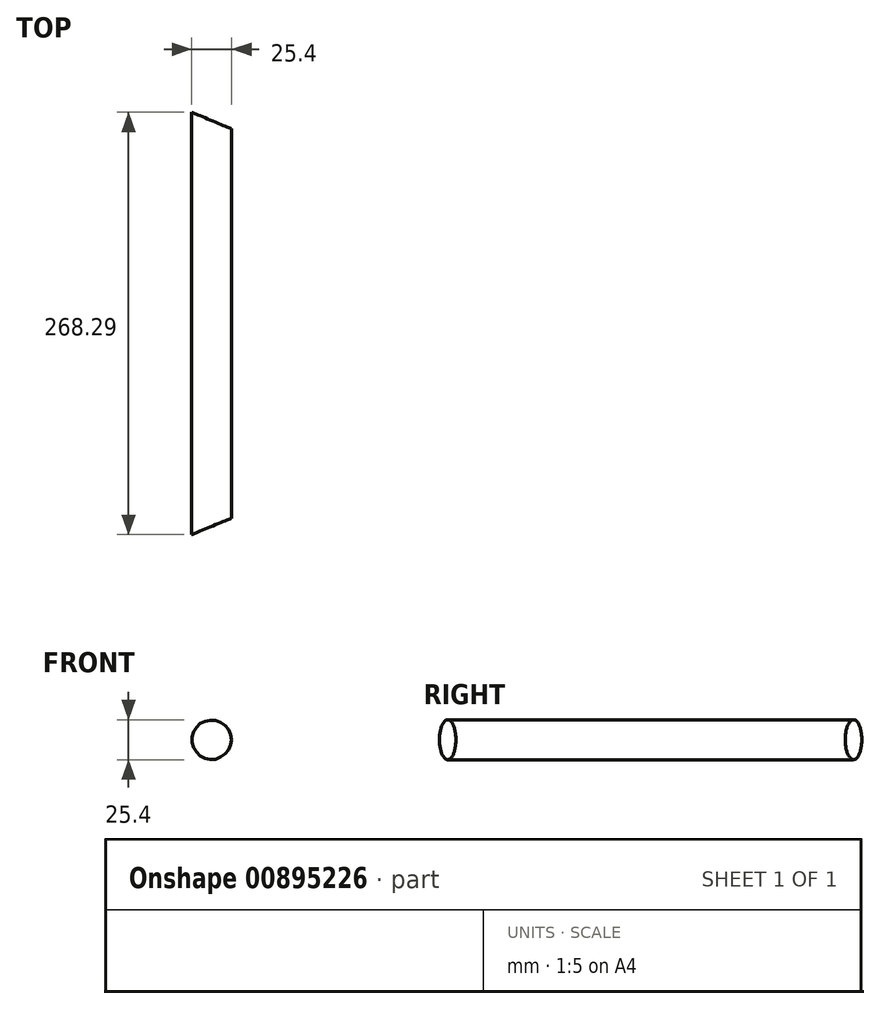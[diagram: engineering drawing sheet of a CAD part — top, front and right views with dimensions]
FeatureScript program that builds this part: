
annotation { "Feature Type Name" : "Feature", "Feature Type Description" : "" }
export const myFeature = defineFeature(function(context is Context, id is Id, definition is map)
    precondition{}
    {
        {
            var Q0;
            Q0=qCreatedBy(makeId("Front.planeOp"),FACE);
            var sketch = newSketch(context, id + "F0", { "sketchPlane" : qUnion([Q0])});
            skCircle(sketch, "E0", {"center": v(0, 0) * mm, "radius": 12.7 * mm});
            skSolve(sketch);
        }
        {
            var Q0;
            Q0=makeQuery(id+"F0.imprint","IMPRINT",FACE,{"disambiguationData":[TD([[makeQuery(id+"F0.imprint","IMPRINT",EDGE,{"derivedFrom":sQuery(id+"F0.wireOp",EDGE,"E0")}),1.0]])]});
            var sketch = newSketch(context, id + "F1", { "sketchPlane" : qUnion([Q0])});
            skSolve(sketch);
        }
        {
            var Q0;
            Q0 = qSketchRegion(id + "F1", true);
            var Q1;
            Q1=makeQuery(id+"F1.imprint","IMPRINT",FACE,{"disambiguationData":[TD([[makeQuery(id+"F1.imprint","IMPRINT",EDGE,{"derivedFrom":makeQuery(id+"F0.imprint","IMPRINT",EDGE,{"derivedFrom":sQuery(id+"F0.wireOp",EDGE,"E0")})}),1.0]])]});
            extrude(context, id + "F2", {"entities" : qUnion([Q0, Q1]), "depth" : 268.3 * mm, "offsetDistance" : 25.4 * mm});
        }
        {
            var Q0;
            Q0=makeQuery(id+"F2.opExtrude","CAP_FACE",FACE,{"disambiguationData":[OSD([sQuery(id+"F0.wireOp",EDGE,"E0")])],"isStart":false});
            cPlane(context, id + "F3", {"entities" : qUnion([Q0]), "cplaneType" : CPlaneType.OFFSET, "offset" : 0 * mm, "width" : 152.4 * mm, "height" : 152.4 * mm});
        }
        {
            var Q0;
            Q0=qCreatedBy(id+"F3.planeOp",FACE);
            var sketch = newSketch(context, id + "F4", { "sketchPlane" : qUnion([Q0])});
            skLineSegment(sketch, "E1.bottom", {"start": v(12.7, 12.7) * mm, "end": v(-12.7, 12.7) * mm});
            skLineSegment(sketch, "E1.top", {"start": v(12.7, -12.7) * mm, "end": v(-12.7, -12.7) * mm});
            skLineSegment(sketch, "E1.left", {"start": v(12.7, 12.7) * mm, "end": v(12.7, -12.7) * mm});
            skLineSegment(sketch, "E1.right", {"start": v(-12.7, 12.7) * mm, "end": v(-12.7, -12.7) * mm});
            skPoint(sketch, "E1.middle", {"position": v(0, 0) * mm});
            skSolve(sketch);
        }
        {
            var Q0;
            Q0=sQuery(id+"F4.wireOp",EDGE,"E1.right");
            cPlane(context, id + "F5", {"entities" : qUnion([Q0]), "cplaneType" : CPlaneType.LINE_ANGLE, "offset" : 25.4 * mm, "angle" : 67.5 * degree, "width" : 152.4 * mm, "height" : 152.4 * mm});
        }
        {
            var Q0;
            Q0=qCreatedBy(id+"F5.planeOp",FACE);
            var sketch = newSketch(context, id + "F6", { "sketchPlane" : qUnion([Q0])});
            skLineSegment(sketch, "E2.bottom", {"start": v(61.14, -41.3) * mm, "end": v(175.23, -41.3) * mm});
            skLineSegment(sketch, "E2.top", {"start": v(61.14, 47.2) * mm, "end": v(175.23, 47.2) * mm});
            skLineSegment(sketch, "E2.left", {"start": v(61.14, -41.3) * mm, "end": v(61.14, 47.2) * mm});
            skLineSegment(sketch, "E2.right", {"start": v(175.23, -41.3) * mm, "end": v(175.23, 47.2) * mm});
            skPoint(sketch, "E2.middle", {"position": v(118.19, 2.95) * mm});
            skSolve(sketch);
        }
        {
            var Q0;
            Q0=makeQuery(id+"F6.imprint","IMPRINT",FACE,{"disambiguationData":[TD([[makeQuery(id+"F6.imprint","IMPRINT",EDGE,{"derivedFrom":sQuery(id+"F6.wireOp",EDGE,"E2.bottom")}),1.0]])]});
            extrude(context, id + "F7", {"entities" : qUnion([Q0]), "operationType" : NewBodyOperationType.REMOVE, "oppositeDirection" : true, "depth" : 25.4 * mm, "offsetDistance" : 25.4 * mm});
        }
        {
            var Q0;
            Q0=makeQuery(id+"F0.imprint","IMPRINT",FACE,{"disambiguationData":[TD([[makeQuery(id+"F0.imprint","IMPRINT",EDGE,{"derivedFrom":sQuery(id+"F0.wireOp",EDGE,"E0")}),1.0]])]});
            cPlane(context, id + "F8", {"entities" : qUnion([Q0]), "cplaneType" : CPlaneType.OFFSET, "offset" : 0 * mm, "width" : 152.4 * mm, "height" : 152.4 * mm});
        }
        {
            var Q0;
            Q0=qCreatedBy(id+"F8.planeOp",FACE);
            var sketch = newSketch(context, id + "F9", { "sketchPlane" : qUnion([Q0])});
            skLineSegment(sketch, "E3.bottom", {"start": v(-12.7, -12.7) * mm, "end": v(12.7, -12.7) * mm});
            skLineSegment(sketch, "E3.top", {"start": v(-12.7, 12.7) * mm, "end": v(12.7, 12.7) * mm});
            skLineSegment(sketch, "E3.left", {"start": v(-12.7, -12.7) * mm, "end": v(-12.7, 12.7) * mm});
            skLineSegment(sketch, "E3.right", {"start": v(12.7, -12.7) * mm, "end": v(12.7, 12.7) * mm});
            skPoint(sketch, "E3.middle", {"position": v(0, 0) * mm});
            skSolve(sketch);
        }
        {
            var Q0;
            Q0=sQuery(id+"F9.wireOp",EDGE,"E3.left");
            cPlane(context, id + "F10", {"entities" : qUnion([Q0]), "cplaneType" : CPlaneType.LINE_ANGLE, "offset" : 25.4 * mm, "angle" : 67.5 * degree, "width" : 152.4 * mm, "height" : 152.4 * mm});
        }
        {
            var Q0;
            Q0=qCreatedBy(id+"F10.planeOp",FACE);
            var sketch = newSketch(context, id + "F11", { "sketchPlane" : qUnion([Q0])});
            skLineSegment(sketch, "E4.bottom", {"start": v(72.83, 41.24) * mm, "end": v(-72.83, 41.24) * mm});
            skLineSegment(sketch, "E4.top", {"start": v(72.83, -41.24) * mm, "end": v(-72.83, -41.24) * mm});
            skLineSegment(sketch, "E4.left", {"start": v(72.83, 41.24) * mm, "end": v(72.83, -41.24) * mm});
            skLineSegment(sketch, "E4.right", {"start": v(-72.83, 41.24) * mm, "end": v(-72.83, -41.24) * mm});
            skPoint(sketch, "E4.middle", {"position": v(0, 0) * mm});
            skSolve(sketch);
        }
        {
            var Q0;
            Q0 = qSketchRegion(id + "F11", true);
            extrude(context, id + "F12", {"entities" : qUnion([Q0]), "operationType" : NewBodyOperationType.REMOVE, "depth" : 25.4 * mm, "offsetDistance" : 25.4 * mm});
        }
    });
